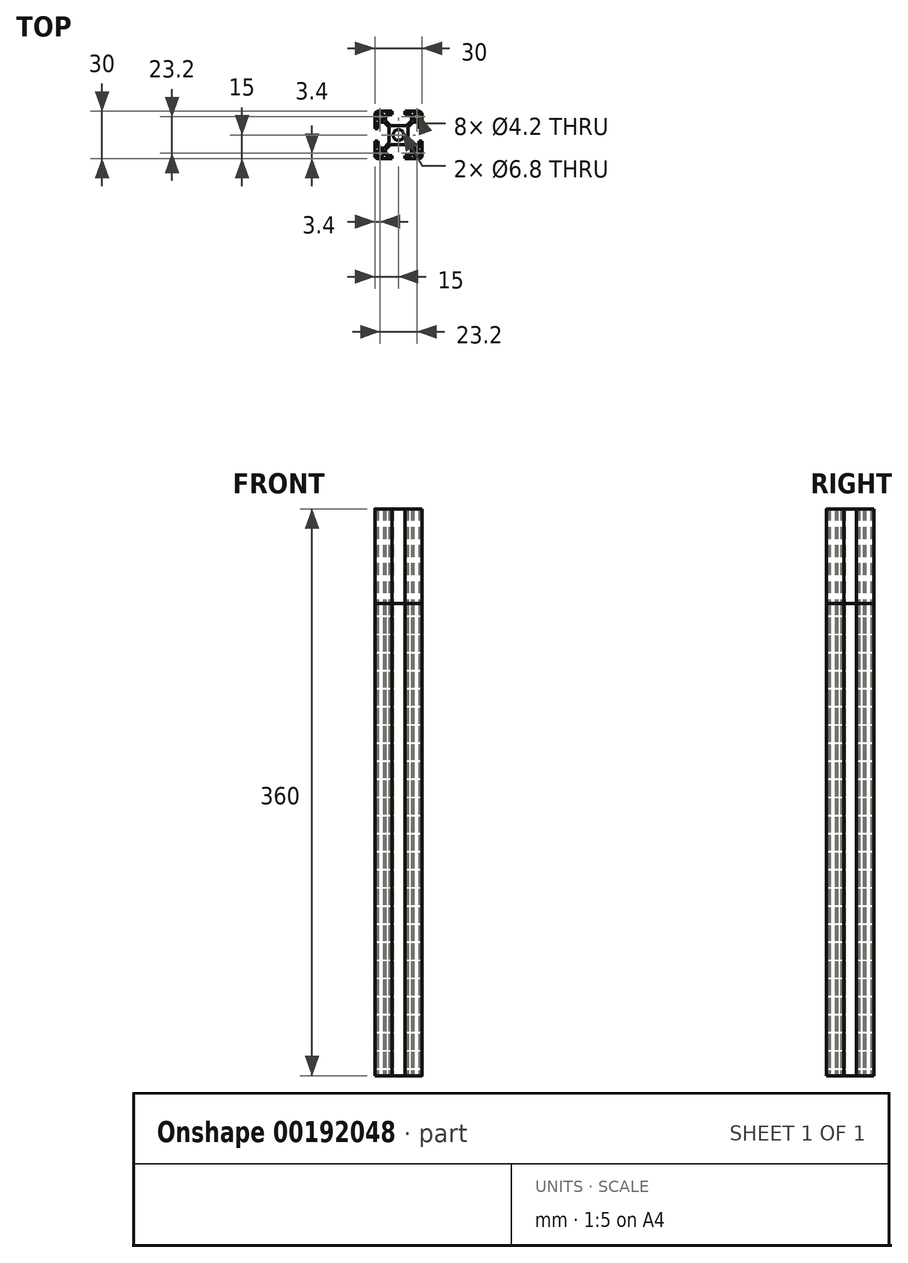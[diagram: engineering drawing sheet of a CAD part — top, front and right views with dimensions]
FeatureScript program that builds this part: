
annotation { "Feature Type Name" : "Feature", "Feature Type Description" : "" }
export const myFeature = defineFeature(function(context is Context, id is Id, definition is map)
    precondition{}
    {
        {
            var Q0;
            Q0=qCreatedBy(makeId("Top.planeOp"),FACE);
            var sketch = newSketch(context, id + "F0", { "sketchPlane" : qUnion([Q0])});
            skLineSegment(sketch, "E0.bottom", {"start": v(15, 15) * mm, "end": v(-15, 15) * mm, "construction": true});
            skLineSegment(sketch, "E0.top", {"start": v(15, -15) * mm, "end": v(-15, -15) * mm, "construction": true});
            skLineSegment(sketch, "E0.left", {"start": v(15, 15) * mm, "end": v(15, -15) * mm, "construction": true});
            skLineSegment(sketch, "E0.right", {"start": v(-15, 15) * mm, "end": v(-15, -15) * mm, "construction": true});
            skPoint(sketch, "E0.middle", {"position": v(0, 0) * mm});
            skLineSegment(sketch, "E1.bottom", {"start": v(6, 6) * mm, "end": v(-6, 6) * mm, "construction": true});
            skLineSegment(sketch, "E1.top", {"start": v(6, -6) * mm, "end": v(-6, -6) * mm, "construction": true});
            skLineSegment(sketch, "E1.left", {"start": v(6, 6) * mm, "end": v(6, -6) * mm, "construction": true});
            skLineSegment(sketch, "E1.right", {"start": v(-6, 6) * mm, "end": v(-6, -6) * mm, "construction": true});
            skLineSegment(sketch, "E2.bottom", {"start": v(11.6, 11.6) * mm, "end": v(-11.6, 11.6) * mm, "construction": true});
            skLineSegment(sketch, "E2.top", {"start": v(11.6, -11.6) * mm, "end": v(-11.6, -11.6) * mm, "construction": true});
            skLineSegment(sketch, "E2.left", {"start": v(11.6, 11.6) * mm, "end": v(11.6, -11.6) * mm, "construction": true});
            skLineSegment(sketch, "E2.right", {"start": v(-11.6, 11.6) * mm, "end": v(-11.6, -11.6) * mm, "construction": true});
            skPoint(sketch, "E3", {"position": v(-4, 15) * mm});
            skPoint(sketch, "E4", {"position": v(4, 15) * mm});
            skPoint(sketch, "E5.1.0", {"position": v(-15, -4) * mm});
            skPoint(sketch, "E5.1.1", {"position": v(-15, 4) * mm});
            skPoint(sketch, "E5.2.0", {"position": v(4, -15) * mm});
            skPoint(sketch, "E5.2.1", {"position": v(-4, -15) * mm});
            skPoint(sketch, "E5.3.0", {"position": v(15, 4) * mm});
            skPoint(sketch, "E5.3.1", {"position": v(15, -4) * mm});
            skLineSegment(sketch, "E6", {"start": v(4, 15) * mm, "end": v(13, 15) * mm});
            skLineSegment(sketch, "E7", {"start": v(15, 4) * mm, "end": v(15, 13) * mm});
            skPoint(sketch, "E8.visualSharp", {"position": v(15, 15) * mm});
            skArc(sketch, "E8.filletArc", {"start": v(15, 13) * mm, "mid": v(14.41, 14.41) * mm, "end": v(13, 15) * mm});
            skLineSegment(sketch, "E9", {"start": v(4, 15) * mm, "end": v(4, 13) * mm});
            skLineSegment(sketch, "E10", {"start": v(4, 13) * mm, "end": v(8.25, 13) * mm});
            skLineSegment(sketch, "E11", {"start": v(15, 4) * mm, "end": v(13, 4) * mm});
            skLineSegment(sketch, "E12", {"start": v(13, 4) * mm, "end": v(13, 8.25) * mm});
            skCircle(sketch, "E13", {"center": v(0, 0) * mm, "radius": 3.4 * mm});
            skLineSegment(sketch, "E14", {"start": v(8.25, 13) * mm, "end": v(8.25, 9.25) * mm});
            skLineSegment(sketch, "E15", {"start": v(8.25, 9.25) * mm, "end": v(5, 6) * mm});
            skLineSegment(sketch, "E16", {"start": v(5, 6) * mm, "end": v(0, 6) * mm});
            skLineSegment(sketch, "E17", {"start": v(13, 8.25) * mm, "end": v(9.25, 8.25) * mm});
            skLineSegment(sketch, "E18", {"start": v(9.25, 8.25) * mm, "end": v(6, 5) * mm});
            skLineSegment(sketch, "E19", {"start": v(6, 5) * mm, "end": v(6, 0) * mm});
            skCircle(sketch, "E20", {"center": v(11.6, 11.6) * mm, "radius": 2.1 * mm});
            skCircle(sketch, "E21.1.0", {"center": v(-11.6, 11.6) * mm, "radius": 2.1 * mm});
            skArc(sketch, "E21.1.1", {"start": v(-13, 15) * mm, "mid": v(-14.41, 14.41) * mm, "end": v(-15, 13) * mm});
            skLineSegment(sketch, "E21.1.2", {"start": v(-4, 15) * mm, "end": v(-4, 13) * mm});
            skLineSegment(sketch, "E21.1.3", {"start": v(-4, 13) * mm, "end": v(-8.25, 13) * mm});
            skLineSegment(sketch, "E21.1.4", {"start": v(-8.25, 13) * mm, "end": v(-8.25, 9.25) * mm});
            skLineSegment(sketch, "E21.1.5", {"start": v(-13, 8.25) * mm, "end": v(-9.25, 8.25) * mm});
            skLineSegment(sketch, "E21.1.6", {"start": v(-13, 4) * mm, "end": v(-13, 8.25) * mm});
            skLineSegment(sketch, "E21.1.7", {"start": v(-9.25, 8.25) * mm, "end": v(-6, 5) * mm});
            skLineSegment(sketch, "E21.1.8", {"start": v(-8.25, 9.25) * mm, "end": v(-5, 6) * mm});
            skLineSegment(sketch, "E21.1.9", {"start": v(-15, 4) * mm, "end": v(-13, 4) * mm});
            skLineSegment(sketch, "E21.1.10", {"start": v(-5, 6) * mm, "end": v(0, 6) * mm});
            skLineSegment(sketch, "E21.1.11", {"start": v(-6, 5) * mm, "end": v(-6, 0) * mm});
            skLineSegment(sketch, "E21.1.12", {"start": v(-4, 15) * mm, "end": v(-13, 15) * mm});
            skLineSegment(sketch, "E21.1.13", {"start": v(-15, 4) * mm, "end": v(-15, 13) * mm});
            skCircle(sketch, "E21.2.0", {"center": v(-11.6, -11.6) * mm, "radius": 2.1 * mm});
            skArc(sketch, "E21.2.1", {"start": v(-15, -13) * mm, "mid": v(-14.41, -14.41) * mm, "end": v(-13, -15) * mm});
            skLineSegment(sketch, "E21.2.2", {"start": v(-15, -4) * mm, "end": v(-13, -4) * mm});
            skLineSegment(sketch, "E21.2.3", {"start": v(-13, -4) * mm, "end": v(-13, -8.25) * mm});
            skLineSegment(sketch, "E21.2.4", {"start": v(-13, -8.25) * mm, "end": v(-9.25, -8.25) * mm});
            skLineSegment(sketch, "E21.2.5", {"start": v(-8.25, -13) * mm, "end": v(-8.25, -9.25) * mm});
            skLineSegment(sketch, "E21.2.6", {"start": v(-4, -13) * mm, "end": v(-8.25, -13) * mm});
            skLineSegment(sketch, "E21.2.7", {"start": v(-8.25, -9.25) * mm, "end": v(-5, -6) * mm});
            skLineSegment(sketch, "E21.2.8", {"start": v(-9.25, -8.25) * mm, "end": v(-6, -5) * mm});
            skLineSegment(sketch, "E21.2.9", {"start": v(-4, -15) * mm, "end": v(-4, -13) * mm});
            skLineSegment(sketch, "E21.2.10", {"start": v(-6, -5) * mm, "end": v(-6, 0) * mm});
            skLineSegment(sketch, "E21.2.11", {"start": v(-5, -6) * mm, "end": v(0, -6) * mm});
            skLineSegment(sketch, "E21.2.12", {"start": v(-15, -4) * mm, "end": v(-15, -13) * mm});
            skLineSegment(sketch, "E21.2.13", {"start": v(-4, -15) * mm, "end": v(-13, -15) * mm});
            skCircle(sketch, "E21.3.0", {"center": v(11.6, -11.6) * mm, "radius": 2.1 * mm});
            skArc(sketch, "E21.3.1", {"start": v(13, -15) * mm, "mid": v(14.41, -14.41) * mm, "end": v(15, -13) * mm});
            skLineSegment(sketch, "E21.3.2", {"start": v(4, -15) * mm, "end": v(4, -13) * mm});
            skLineSegment(sketch, "E21.3.3", {"start": v(4, -13) * mm, "end": v(8.25, -13) * mm});
            skLineSegment(sketch, "E21.3.4", {"start": v(8.25, -13) * mm, "end": v(8.25, -9.25) * mm});
            skLineSegment(sketch, "E21.3.5", {"start": v(13, -8.25) * mm, "end": v(9.25, -8.25) * mm});
            skLineSegment(sketch, "E21.3.6", {"start": v(13, -4) * mm, "end": v(13, -8.25) * mm});
            skLineSegment(sketch, "E21.3.7", {"start": v(9.25, -8.25) * mm, "end": v(6, -5) * mm});
            skLineSegment(sketch, "E21.3.8", {"start": v(8.25, -9.25) * mm, "end": v(5, -6) * mm});
            skLineSegment(sketch, "E21.3.9", {"start": v(15, -4) * mm, "end": v(13, -4) * mm});
            skLineSegment(sketch, "E21.3.10", {"start": v(5, -6) * mm, "end": v(0, -6) * mm});
            skLineSegment(sketch, "E21.3.11", {"start": v(6, -5) * mm, "end": v(6, 0) * mm});
            skLineSegment(sketch, "E21.3.12", {"start": v(4, -15) * mm, "end": v(13, -15) * mm});
            skLineSegment(sketch, "E21.3.13", {"start": v(15, -4) * mm, "end": v(15, -13) * mm});
            skSolve(sketch);
        }
        {
            var Q0;
            Q0 = qSketchRegion(id + "F0", true);
            extrude(context, id + "F1", {"entities" : qUnion([Q0]), "depth" : 300 * mm});
        }
        {
            var Q0;
            Q0 = qSketchRegion(id + "F0", true);
            extrude(context, id + "F2", {"entities" : qUnion([Q0]), "depth" : 360 * mm});
        }
    });
